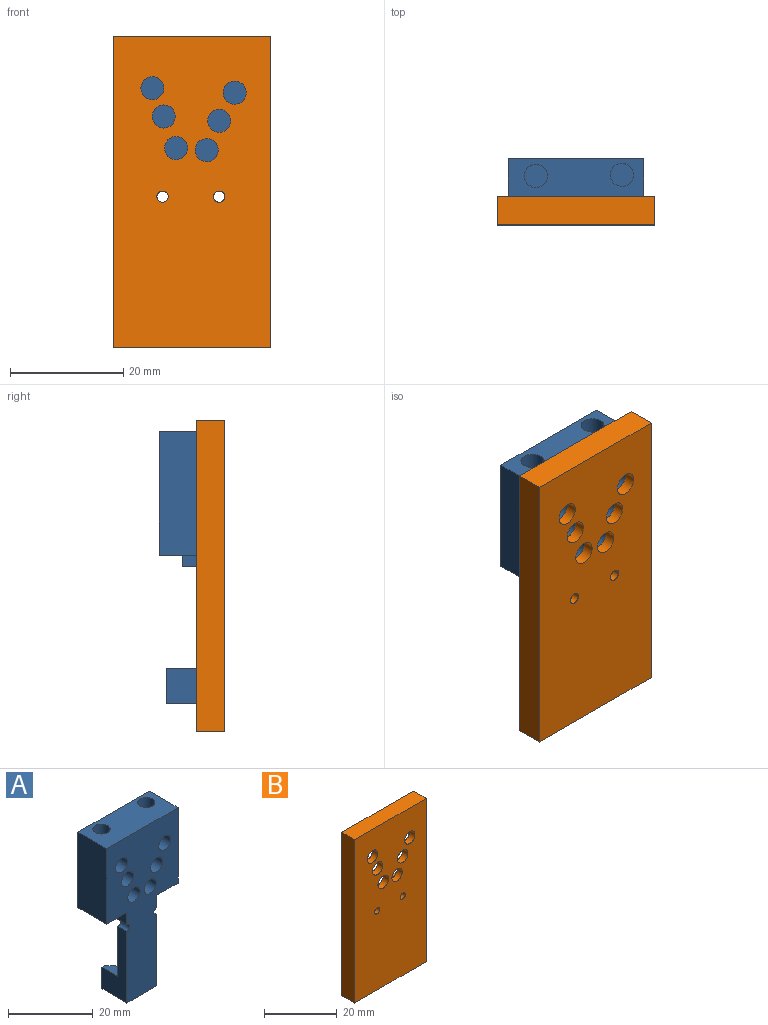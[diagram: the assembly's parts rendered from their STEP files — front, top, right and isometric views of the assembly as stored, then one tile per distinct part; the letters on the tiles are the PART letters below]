
ASSEMBLY  parts=2 mates=1
PART A: 120 faces, bbox 24.4x10.2x48.6 mm
  f0: plane 5.56x3.5mm, normal (-1,0,0), area 15.6mm2, adj f4,f5,f40,f84,f116,f119
  f1: plane 20.7x8.35mm, normal (1,0,0), area 95.3mm2, adj f4,f84,f104,f105,f109,f118
  f2: plane 14.35x10.14mm, normal (0,0,-1), area 83.4mm2, adj f6,f10,f40,f42,f43,f45,f82,f84
  f3: plane 6.2x4.6mm, normal (0,1,0), area 15.5mm2, adj f104,f105,f106,f108,f110
  f4: plane 18x10mm, normal (0,1,0), area 176.9mm2, adj f0,f1,f102,f103,f105,f116,f118,f119
  f5: plane 9.89x9.68mm, normal (0,0,-1), area 75.8mm2, adj f0,f39,f40,f41,f43,f60,f84
  f6: plane 1.06x0.33mm, normal (-0.9,0,-0.44), area 0.4mm2, adj f2,f7,f9,f10,f14,f15,f40,f51
  f7: plane 2.08x0.95mm, normal (-0.91,0,-0.42), area 0.2mm2, adj f6,f10,f11,f12,f14,f19
  f8: bspline ~0.75x0.45mm, area 0mm2, adj f36,f38,f52
  f9: cone r=179.19mm half-angle=55deg, axis (-0.91,0,-0.42), area 0mm2, adj f6,f11,f14,f15,f51
  f10: cylinder r=5.23mm len=3.77mm, axis (-0.91,0,0.42), area 3.2mm2, adj f2,f6,f7,f12,f33,f45
  f11: cylinder r=177.1mm len=2.19mm, axis (-0.94,0,-0.35), area 0mm2, adj f7,f9,f14
  f12: cylinder r=2mm len=3.29mm, axis (-0.91,0,0.42), area 1mm2, adj f7,f10,f16,f20,f32,f33
  f13: bspline ~0.33x0.28mm, area 0mm2, adj f35,f36,f38,f53
  f14: cylinder r=5.1mm len=0.18mm, axis (0.94,0,0.35), area 0mm2, adj f6,f7,f9,f11,f15
  f15: plane 0.15x0.07mm, normal (0,-1,0), area 0mm2, adj f6,f9,f14
  f16: cylinder r=22.95mm len=15.51mm, axis (-0.91,0,0.42), area 41.5mm2, adj f12,f21,f22,f23,f24,f29,f30,f32
  f17: cylinder r=3.59mm len=0.92mm, axis (0,-1,0), area 0.7mm2, adj f18,f56,f67,f83
  f18: plane 6.12x3.03mm, normal (-0.91,0,-0.42), area 14.4mm2, adj f17,f19,f68,f83
  f19: plane 7.29x3.41mm, normal (-0.91,0,-0.42), area 24.7mm2, adj f7,f18,f20,f38,f51,f52,f69,f83
  f20: plane 2.17x0.19mm, normal (0.87,0,-0.49), area 0.5mm2, adj f12,f19,f21,f70
  f21: plane 10.87x6.05mm, normal (0.87,0,-0.49), area 38.7mm2, adj f16,f20,f46,f71
  f22: cylinder r=0.16mm len=2.05mm, axis (0,-1,0), area 0.1mm2, adj f16,f48,f50,f75
  f23: cylinder r=2.51mm len=2.01mm, axis (0,1,0), area 0.3mm2, adj f16,f24,f48,f77
  f24: cylinder r=0.93mm len=2.02mm, axis (0,1,0), area 0.2mm2, adj f16,f23,f25,f49,f78
  f25: cylinder r=1.53mm len=1.95mm, axis (0,-1,0), area 2.9mm2, adj f24,f29,f79
  f26: cylinder r=0.15mm len=0.23mm, axis (0,1,0), area 0mm2, adj f27,f44,f58,f63
  f27: plane 0.22x0.02mm, normal (0.1,0,-1), area 0mm2, adj f26,f28,f57,f64
  f28: plane 0.84x0.13mm, normal (0.07,0,-1), area 0.1mm2, adj f27,f36,f55,f56,f57,f58,f65
  f29: cylinder r=1.53mm len=2.5mm, axis (0,1,0), area 1.6mm2, adj f16,f25,f30,f49,f80
  f30: plane 12.88x5.53mm, normal (-0.92,0,0.39), area 42.9mm2, adj f16,f29,f33,f81
  f31: plane 13.27x4.49mm, normal (0.95,0,0.32), area 43.7mm2, adj f34,f36,f44,f61
  f32: cylinder r=0.1mm len=0.01mm, axis (-0.38,0.31,-0.87), area 0mm2, adj f12,f16
  f33: cylinder r=1.02mm len=2.16mm, axis (0,1,0), area 2.2mm2, adj f10,f12,f30,f45,f82
  f34: cylinder r=1.02mm len=3.15mm, axis (0,1,0), area 3.3mm2, adj f31,f36,f37,f38,f53,f60
  f35: bspline ~0.58x0.34mm, area 0mm2, adj f13,f36,f38
  f36: cylinder r=22.44mm len=15.71mm, axis (-0.94,0,-0.35), area 35.8mm2, adj f8,f13,f28,f31,f34,f35,f38,f44
  f37: cylinder r=0.41mm len=3.59mm, axis (0,1,0), area 2.3mm2, adj f34,f38,f39,f40,f60
  f38: cylinder r=10.2mm len=3.97mm, axis (-0.94,0,-0.35), area 5.4mm2, adj f8,f13,f19,f34,f35,f36,f37,f40
  f39: cylinder r=3.06mm len=3.76mm, axis (0,1,0), area 0.7mm2, adj f5,f37,f40,f60
  f40: plane 6.22x3.6mm, normal (0,1,0), area 8.9mm2, adj f0,f2,f5,f6,f37,f38,f39,f51
  f41: plane 21.85x9.64mm, normal (-1,0,0), area 210.7mm2, adj f5,f43,f84,f97
  f42: plane 21.85x9.64mm, normal (1,0,0), area 210.7mm2, adj f2,f43,f84,f97
  f43: plane 23.94x21.9mm, normal (0,1,0), area 361.6mm2, adj f2,f5,f41,f42,f60,f61,f62,f63
  f44: cylinder r=1.53mm len=1.87mm, axis (0,1,0), area 2.5mm2, adj f26,f31,f36,f54,f59,f62
  f45: cylinder r=0.41mm len=2.51mm, axis (0,1,0), area 1.5mm2, adj f2,f10,f33,f82
  f46: plane 2.92x1.15mm, normal (0.85,0,-0.52), area 3.6mm2, adj f16,f21,f47,f72
  f47: plane 2.58x0.56mm, normal (0.82,0,-0.58), area 1.7mm2, adj f16,f46,f50,f73
  f48: extruded ~2.03x0.19mm, area 0.4mm2, adj f16,f22,f23,f76
  f49: cylinder r=1.53mm len=1.42mm, axis (0,1,0), area 0.1mm2, adj f16,f24,f29
  f50: cylinder r=15.82mm len=2.38mm, axis (0,1,0), area 2.2mm2, adj f16,f22,f47,f74
  f51: plane 2.08x1.04mm, normal (-0.91,0,-0.42), area 2.2mm2, adj f6,f9,f19,f38,f40
  f52: plane 0.77x0.46mm, normal (0.35,0,-0.94), area 0.1mm2, adj f8,f19,f36,f38,f83
  f53: plane 0.19x0.07mm, normal (0.35,0,-0.94), area 0mm2, adj f13,f34,f36,f38
  f54: cylinder r=0.15mm len=0.58mm, axis (0,1,0), area 0mm2, adj f36,f44,f55,f58,f59
  f55: plane 0.57x0.02mm, normal (0.1,0,-1), area 0mm2, adj f28,f36,f54,f58
  f56: extruded ~0.84x0.18mm, area 0.1mm2, adj f17,f28,f66,f83
  f57: cylinder r=0.2mm len=0.16mm, axis (0.58,0.81,0.04), area 0mm2, adj f27,f28,f58
  f58: cylinder r=0.21mm len=0.09mm, axis (0.59,0.8,0.05), area 0mm2, adj f26,f28,f54,f55,f57,f59
  f59: bspline ~0.41x0.26mm, area 0mm2, adj f44,f54,f58
  f60: cone r=2.02mm half-angle=45deg, axis (0,1,0), area 2.5mm2, adj f5,f34,f37,f39,f43,f61
  f61: plane 13.58x5.43mm, normal (0.67,0.71,0.23), area 19.8mm2, adj f31,f43,f60,f62
  f62: cone r=2.53mm half-angle=45deg, axis (0,1,0), area 4.1mm2, adj f43,f44,f61,f63
  f63: cone r=1.15mm half-angle=45deg, axis (0,1,0), area 0.4mm2, adj f26,f43,f62,f64
  f64: plane 1.02x1.02mm, normal (0.07,0.71,-0.7), area 0mm2, adj f27,f43,f63,f65
  f65: plane 1.04x1.03mm, normal (0.05,0.71,-0.71), area 0.2mm2, adj f28,f43,f64,f66
  f66: bspline ~1.06x1.02mm, area 0.9mm2, adj f43,f56,f65,f67
  f67: cone r=3.59mm half-angle=45deg, axis (0,1,0), area 1.4mm2, adj f17,f43,f66,f68
  f68: plane 6.5x3.73mm, normal (-0.64,0.71,-0.3), area 9.5mm2, adj f18,f43,f67,f69
  f69: plane 7.66x3.44mm, normal (-0.64,0.71,-0.3), area 9.9mm2, adj f19,f43,f68,f70,f71
  f70: plane 0.24x0.11mm, normal (0.62,0.71,-0.34), area 0mm2, adj f20,f69,f71
  f71: plane 11.36x6.15mm, normal (0.62,0.71,-0.34), area 16.5mm2, adj f21,f43,f69,f70,f72
  f72: plane 1.66x1.57mm, normal (0.6,0.71,-0.37), area 1.9mm2, adj f43,f46,f71,f73
  f73: plane 1.25x1.15mm, normal (0.58,0.71,-0.41), area 1mm2, adj f43,f47,f72,f74
  f74: bspline ~1.42x1.42mm, area 1.4mm2, adj f43,f50,f73,f75
  f75: cone r=0.16mm half-angle=45deg, axis (0,1,0), area 0.4mm2, adj f22,f43,f74,f76
  f76: bspline ~1.1x1.05mm, area 0.9mm2, adj f43,f48,f75,f77
  f77: cone r=3.51mm half-angle=45deg, axis (0,1,0), area 0.3mm2, adj f23,f43,f76,f78
  f78: cone r=1.93mm half-angle=45deg, axis (0,1,0), area 0.3mm2, adj f24,f43,f77,f79
  f79: cone r=1.53mm half-angle=45deg, axis (0,1,0), area 3mm2, adj f25,f43,f78,f80
  f80: cone r=2.53mm half-angle=45deg, axis (0,1,0), area 0.8mm2, adj f29,f43,f79,f81
  f81: plane 13.27x6.45mm, normal (-0.65,0.71,0.28), area 19.8mm2, adj f30,f43,f80,f82
  f82: cone r=2.02mm half-angle=45deg, axis (0,1,0), area 2.2mm2, adj f2,f33,f43,f45,f81
  f83: bspline ~15.58x7.4mm, area 7.5mm2, adj f17,f18,f19,f36,f52,f56
  f84: plane 48.05x23.89mm, normal (0,-1,0), area 702.8mm2, adj f0,f1,f2,f5,f41,f42,f85,f87
  f85: cylinder r=2.03mm len=4.2mm, axis (0,-1,0), area 53.7mm2, adj f84,f86
  f86: plane 4.07x4.07mm, normal (0,-1,0), area 13mm2, adj f85
  f87: cylinder r=2.03mm len=4.2mm, axis (0,-1,0), area 53.7mm2, adj f84,f88
  f88: plane 4.07x4.07mm, normal (0,-1,0), area 13mm2, adj f87
  f89: cylinder r=2.03mm len=4.2mm, axis (0,-1,0), area 53.7mm2, adj f84,f90
  f90: plane 4.07x4.07mm, normal (0,-1,0), area 13mm2, adj f89
  f91: cylinder r=2.03mm len=4.2mm, axis (0,-1,0), area 53.7mm2, adj f84,f92
  f92: plane 4.07x4.07mm, normal (0,-1,0), area 13mm2, adj f91
  f93: cylinder r=2.03mm len=4.2mm, axis (0,-1,0), area 53.7mm2, adj f84,f94
  f94: plane 4.07x4.07mm, normal (0,-1,0), area 13mm2, adj f93
  f95: cylinder r=2.03mm len=4.2mm, axis (0,-1,0), area 53.7mm2, adj f84,f96
  f96: plane 4.07x4.07mm, normal (0,-1,0), area 13mm2, adj f95
  f97: plane 23.89x9.64mm, normal (0,0,1), area 204.3mm2, adj f41,f42,f43,f84,f98,f100
  f98: cylinder r=2.03mm len=4.2mm, axis (0,0,1), area 53.7mm2, adj f97,f99
  f99: plane 4.07x4.07mm, normal (0,0,1), area 13mm2, adj f98
  f100: cylinder r=2.03mm len=4.2mm, axis (0,0,1), area 53.7mm2, adj f97,f101
  f101: plane 4.07x4.07mm, normal (0,0,1), area 13mm2, adj f100
  f102: plane 20.7x8.35mm, normal (-1,0,0), area 95.3mm2, adj f4,f84,f104,f105,f111,f119
  f103: plane 5.56x3.5mm, normal (1,0,0), area 15.6mm2, adj f2,f4,f84,f115,f116,f118
  f104: plane 10x8.35mm, normal (0,0,-1), area 62mm2, adj f1,f3,f84,f102,f108,f109,f110,f111
  f105: plane 10x5.35mm, normal (0,0,1), area 32mm2, adj f1,f3,f4,f102,f108,f109,f110,f111
  f106: cylinder r=2.03mm len=4.07mm, axis (0,1,0), area 28.1mm2, adj f3,f107
  f107: plane 4.07x4.07mm, normal (0,1,0), area 13mm2, adj f106
  f108: plane 6.2x2.25mm, normal (-1,0,0), area 13.9mm2, adj f3,f104,f105,f113
  f109: plane 6.2x0.95mm, normal (0,1,0), area 5.9mm2, adj f1,f104,f105,f113
  f110: plane 6.2x2.25mm, normal (1,0,0), area 13.9mm2, adj f3,f104,f105,f112
  f111: plane 6.2x0.95mm, normal (0,1,0), area 5.9mm2, adj f102,f104,f105,f112
  f112: plane 6.2x1.75mm, normal (0.71,0.71,0), area 15.3mm2, adj f104,f105,f110,f111
  f113: plane 6.2x1.75mm, normal (-0.71,0.71,0), area 15.3mm2, adj f104,f105,f108,f109
  f114: cylinder r=2mm len=3.42mm, axis (0,0,1), area 4.1mm2, adj f2,f40,f115,f117
  f115: plane 3.39x2.1mm, normal (0,1,0), area 6mm2, adj f2,f103,f114,f116,f117
  f116: plane 10x2.56mm, normal (0,0,-1), area 17.6mm2, adj f0,f4,f40,f103,f115,f117
  f117: cone r=2mm half-angle=45deg, axis (0,0,-1), area 8mm2, adj f40,f114,f115,f116
  f118: cylinder r=1mm len=3mm, axis (0,1,0), area 9.4mm2, adj f1,f4,f84,f103
  f119: cylinder r=1mm len=3mm, axis (0,1,0), area 9.4mm2, adj f0,f4,f84,f102
PART B: 25 faces, bbox 27.9x5x55.1 mm
  f0: plane 20.7x3mm, normal (-1,0,0), area 62.1mm2, adj f2,f9,f15,f24
  f1: plane 20.7x3mm, normal (1,0,0), area 62.1mm2, adj f2,f9,f15,f23
  f2: plane 55.05x27.89mm, normal (0,1,0), area 748.1mm2, adj f0,f1,f3,f4,f5,f6,f7,f8
  f3: plane 6.75x3mm, normal (0,0,1), area 20.2mm2, adj f2,f4,f14,f15
  f4: plane 21.85x3mm, normal (1,0,0), area 65.6mm2, adj f2,f3,f5,f15
  f5: plane 23.89x3mm, normal (0,0,-1), area 71.7mm2, adj f2,f4,f6,f15
  f6: plane 21.85x3mm, normal (-1,0,0), area 65.6mm2, adj f2,f5,f7,f15
  f7: plane 7.14x3mm, normal (0,0,1), area 21.4mm2, adj f2,f6,f8,f15
  f8: plane 3.5x3mm, normal (-1,0,0), area 10.5mm2, adj f2,f7,f15,f24
  f9: plane 10x3mm, normal (0,0,1), area 30mm2, adj f0,f1,f2,f15
  f10: plane 27.89x5mm, normal (0,0,1), area 139.4mm2, adj f2,f11,f13,f22
  f11: plane 55.05x5mm, normal (-1,0,0), area 275.3mm2, adj f2,f10,f12,f22
  f12: plane 27.89x5mm, normal (0,0,-1), area 139.4mm2, adj f2,f11,f13,f22
  f13: plane 55.05x5mm, normal (1,0,0), area 275.3mm2, adj f2,f10,f12,f22
  f14: plane 3.5x3mm, normal (1,0,0), area 10.5mm2, adj f2,f3,f15,f23
  f15: plane 48.05x23.89mm, normal (0,1,0), area 702.8mm2, adj f0,f1,f3,f4,f5,f6,f7,f8
  f16: cylinder r=2.03mm len=4.07mm, axis (0,1,0), area 25.6mm2, adj f15,f22
  f17: cylinder r=2.03mm len=4.07mm, axis (0,1,0), area 25.6mm2, adj f15,f22
  f18: cylinder r=2.03mm len=4.07mm, axis (0,1,0), area 25.6mm2, adj f15,f22
  f19: cylinder r=2.03mm len=4.07mm, axis (0,1,0), area 25.6mm2, adj f15,f22
  f20: cylinder r=2.03mm len=4.07mm, axis (0,1,0), area 25.6mm2, adj f15,f22
  f21: cylinder r=2.03mm len=4.07mm, axis (0,1,0), area 25.6mm2, adj f15,f22
  f22: plane 55.05x27.89mm, normal (0,-1,0), area 1450.9mm2, adj f10,f11,f12,f13,f16,f17,f18,f19
  f23: cylinder r=1mm len=5mm, axis (0,1,0), area 22mm2, adj f1,f2,f14,f15,f22
  f24: cylinder r=1mm len=5mm, axis (0,1,0), area 22mm2, adj f0,f2,f8,f15,f22
PLACE A at identity
PLACE B at identity fixed
MATE fastened A.f84 <-> B.f15  axis (0,-1,0) through (-12.73,-5.5,-2.07)mm
